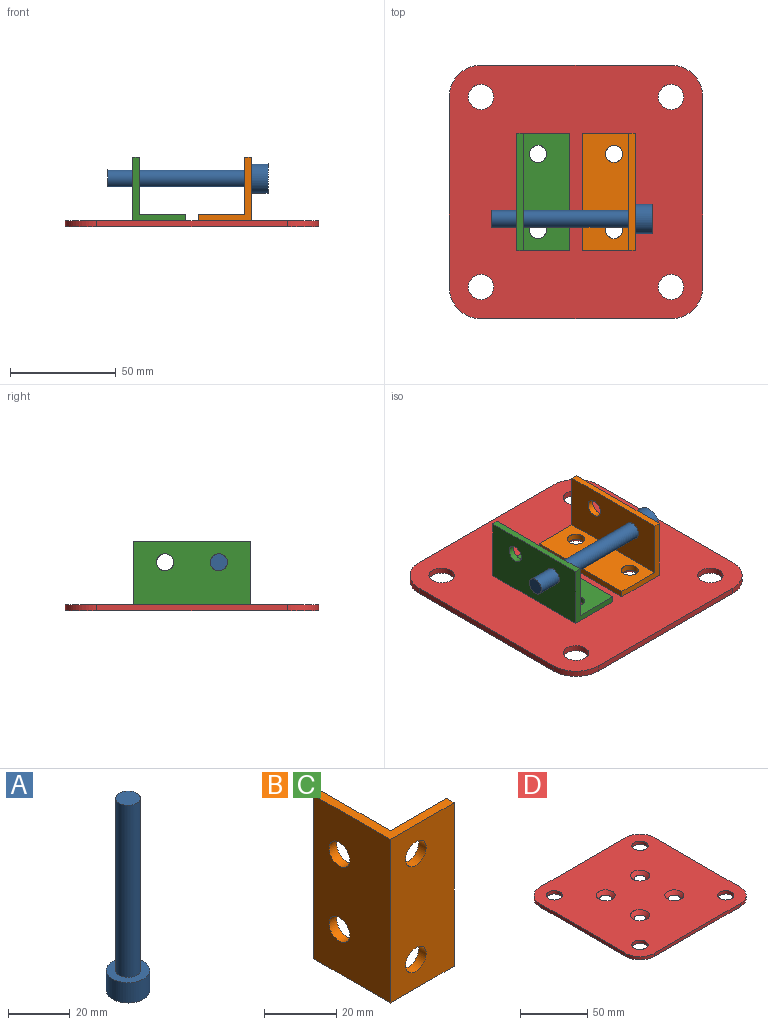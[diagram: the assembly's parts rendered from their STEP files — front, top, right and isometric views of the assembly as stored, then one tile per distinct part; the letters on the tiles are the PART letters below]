
ASSEMBLY  parts=4 mates=2
PART A: 5 faces, bbox 14x14x76 mm
  f0: cylinder r=7mm len=14mm, axis (0,0,-1), area 351.9mm2, adj f1,f2
  f1: plane 14x14mm, normal (0,0,1), area 103.7mm2, adj f0,f3
  f2: plane 14x14mm, normal (0,0,-1), area 153.9mm2, adj f0
  f3: cylinder r=4mm len=68mm, axis (0,0,-1), area 1709mm2, adj f1,f4
  f4: plane 8x8mm, normal (0,0,1), area 50.3mm2, adj f3
PART B: 12 faces, bbox 25x30x55.5 mm
  f0: plane 55.5x3mm, normal (0,1,0), area 166.5mm2, adj f1,f5,f6,f7
  f1: plane 55.5x30mm, normal (-1,0,0), area 1561.9mm2, adj f0,f2,f6,f7,f8,f9
  f2: plane 55.5x25mm, normal (0,-1,0), area 1284.4mm2, adj f1,f3,f6,f7,f10,f11
  f3: plane 55.5x3mm, normal (1,0,0), area 166.5mm2, adj f2,f4,f6,f7
  f4: plane 55.5x22mm, normal (0,1,0), area 1117.9mm2, adj f3,f5,f6,f7,f10,f11
  f5: plane 55.5x27mm, normal (1,0,0), area 1395.4mm2, adj f0,f4,f6,f7,f8,f9
  f6: plane 30x25mm, normal (0,0,1), area 156mm2, adj f0,f1,f2,f3,f4,f5
  f7: plane 30x25mm, normal (0,0,-1), area 156mm2, adj f0,f1,f2,f3,f4,f5
  f8: cylinder r=4.05mm len=8.1mm, axis (-1,0,0), area 76.3mm2, adj f1,f5
  f9: cylinder r=4.05mm len=8.1mm, axis (-1,0,0), area 76.3mm2, adj f1,f5
  f10: cylinder r=4.05mm len=8.1mm, axis (0,-1,0), area 76.3mm2, adj f2,f4
  f11: cylinder r=4.05mm len=8.1mm, axis (0,-1,0), area 76.3mm2, adj f2,f4
PART C: same geometry as B
PART D: 18 faces, bbox 120x120x3 mm
  f0: plane 90x3mm, normal (1,0,0), area 270mm2, adj f1,f11,f12,f13
  f1: cylinder r=15mm len=15mm, axis (0,0,-1), area 70.7mm2, adj f0,f2,f12,f13
  f2: plane 90x3mm, normal (0,1,0), area 270mm2, adj f1,f3,f12,f13
  f3: cylinder r=15mm len=15mm, axis (0,0,-1), area 70.7mm2, adj f2,f4,f12,f13
  f4: plane 90x3mm, normal (-1,0,0), area 270mm2, adj f3,f5,f12,f13
  f5: cylinder r=15mm len=15mm, axis (0,0,-1), area 70.7mm2, adj f4,f6,f12,f13
  f6: plane 90x3mm, normal (0,-1,0), area 270mm2, adj f5,f11,f12,f13
  f7: cylinder r=6mm len=12mm, axis (0,0,-1), area 113.1mm2, adj f12,f13
  f8: cylinder r=6mm len=12mm, axis (0,0,-1), area 113.1mm2, adj f12,f13
  f9: cylinder r=6mm len=12mm, axis (0,0,-1), area 113.1mm2, adj f12,f13
  f10: cylinder r=6mm len=12mm, axis (0,0,-1), area 113.1mm2, adj f12,f13
  f11: cylinder r=15mm len=15mm, axis (0,0,-1), area 70.7mm2, adj f0,f6,f12,f13
  f12: plane 120x120mm, normal (0,0,1), area 13129.9mm2, adj f0,f1,f2,f3,f4,f5,f6,f7
  f13: plane 120x120mm, normal (0,0,-1), area 13506.5mm2, adj f0,f1,f2,f3,f4,f5,f6,f7
  f14: cone r=4.05mm half-angle=41deg, axis (0,0,1), area 143.5mm2, adj f12,f13
  f15: cone r=4.05mm half-angle=41deg, axis (0,0,1), area 143.5mm2, adj f12,f13
  f16: cone r=4.05mm half-angle=41deg, axis (0,0,1), area 143.5mm2, adj f12,f13
  f17: cone r=4.05mm half-angle=41deg, axis (0,0,1), area 143.5mm2, adj f12,f13
PLACE A rot(axis=(-0.71,0,0.71),180deg) t=(20.52,7.92,40.03)mm
PLACE B rot(axis=(0,-0.71,-0.71),180deg) t=(4.55,-7.08,23.34)mm
PLACE C rot(axis=(1,0,0),90deg) t=(-35.57,48.42,23.34)mm
PLACE D rot(axis=(1,0,0),180deg) t=(-15.51,20.67,20.03)mm
MATE slider A.f3 <-> C.f8  axis (-1,0,0) through (-55.48,7.92,40.03)mm
MATE fastened D.f17 <-> C.f10  axis (0,0,1) through (-33.51,38.67,20.03)mm
